# Revit family: PRD_FrankeWS_Mrrs_ContinaMirror_CNTX91
name_source: partatom
category: Furniture
revit_build: Autodesk Revit 2018 (Build: 20190510_1515(x64)
units: mm (PartAtom-declared; Revit-internal decimal feet)

## family parameters
Cut with Voids When Loaded = No
Host = Face
OmniClass Number = 23.40.20.21
OmniClass Title = Toilet and Bath Specialties
Room Calculation Point = No
Shared = No

## types (1)
- CNTX91
    AssetType = Fixed
    BIMObjectName = PRD_AR_Mirrors_ContinaMirror_CNTX91
    Category = Pr_25_71_53_06, Bathroom mirrors
    Color = Stainless steel
    Default Elevation = 1100 mm
    Description = Swingable mirror for wall mounting, mirror and brackets stainless steel, mirror with a reflective polished surface, brackets surface satin finished, reinforced with polystyrene plate and hidden fixings, reinforced 1.5 mm stainless steel bracket on backside, swingable due to premounted lever, lever can be mounted right or left, incl. stainless steel screws and dowels.
    DurationUnit = year
    Features = swingable, stainless steel, 1.00 mm, high polished, wall mounting, 600x500x74 mm (WxHxD)
    Finish = High polished
    Form = Wall mounted
    FrameMaterial = PRD_AR_StainlessSteel_SatinFinished
    GrossWeight = 8.00 kg
    IfcExportAs = IfcFurnitureType
    IfcExportType = NOTDEFINED
    IntegralAccessories = Stainless steel screws and dowels incl.
    MainColor = Stainless steel
    Manufacturer = KWC Group AG
    ManufacturerName = KWC Group AG
    ManufacturerURL = www.kwc.com
    Material = Stainless steel
    MaterialsFrame = Polystyrene
    MaterialsGlazing = Stainless steel 1.4301
    MirrorMaterial = PRD_AR_StainlessSteel_HighPolished
    Model = CNTX91
    ModelNumber = 2000057509
    ModelReference = CNTX91
    NBSDescription = Mirrors
    NBSReference = 45-35-72/336
    Name = CONTINA mirror CNTX91
    NetWeight = 7.50 kg
    NominalDepth = 74 mm  [stored 0.242782 ft]
    NominalHeight = 500 mm  [stored 1.64042 ft]
    NominalLength = 600 mm
    NominalWidth = 600 mm
    ProductInformation = https://pim.kwc.com
    Size = 600 x 500 x 74 mm
    Style = Mirror
    TypeOfFixing = Clamp
    URL = www.kwc.com
    Uniclass2015Code = Pr_25_71_53_06
    Uniclass2015Title = Bathroom mirrors
    Uniclass2015Version = Products v1.5
    Version = 1
    WarrantyDurationUnit = year

note: [stored X ft] marks values corroborated as IEEE doubles in the binary element streams (Revit-internal decimal feet)

## geometry (parser evidence)
native form markers: Sweep x4
no freeform markers — native parametric forms only
